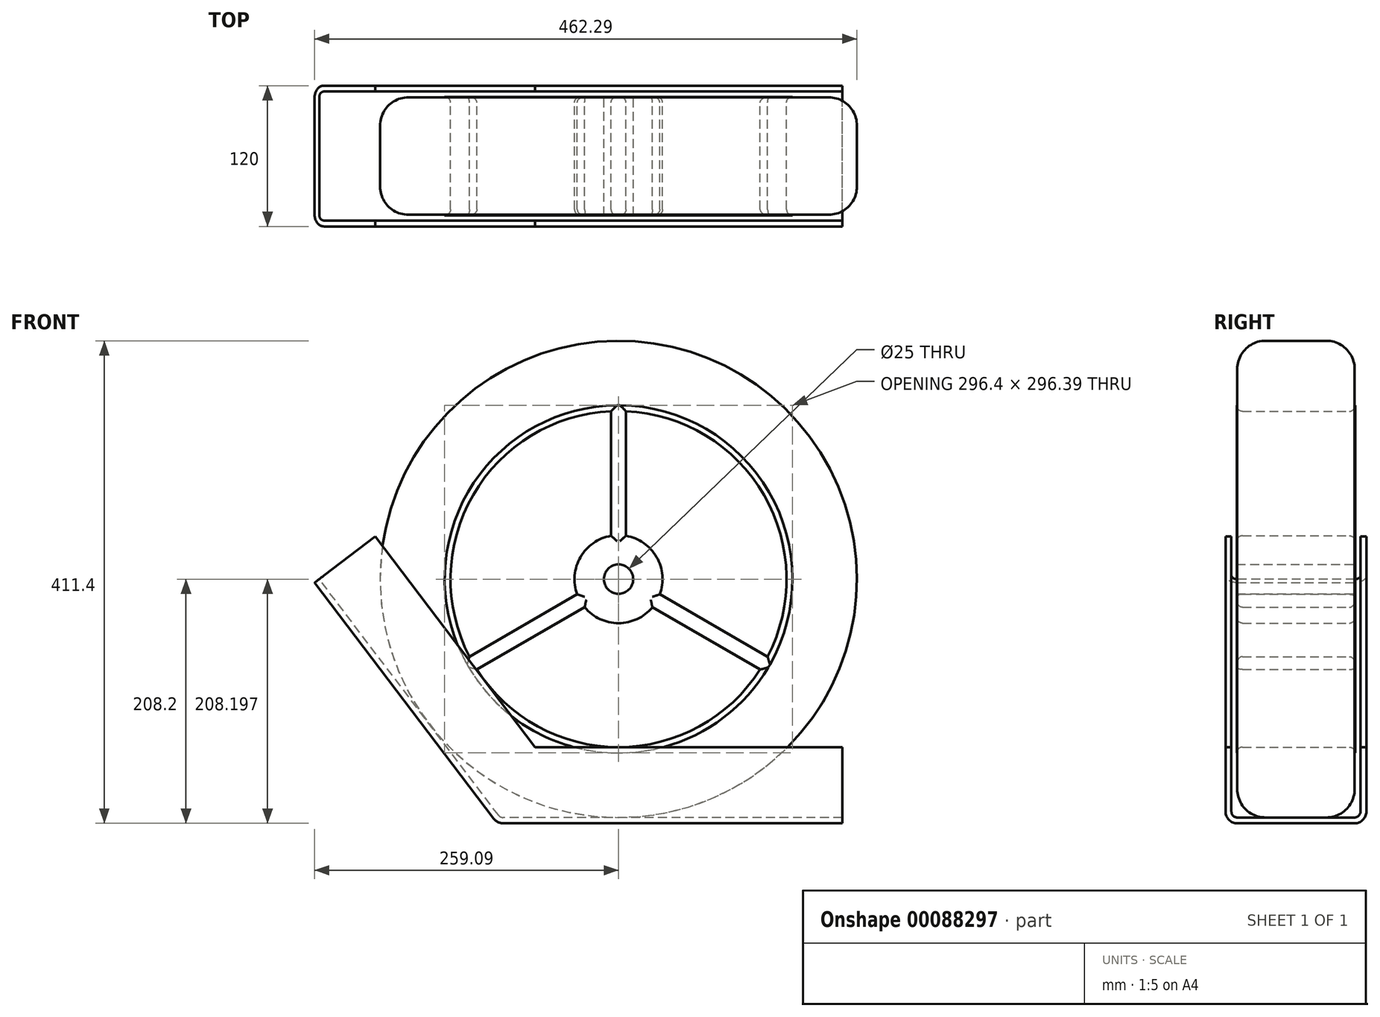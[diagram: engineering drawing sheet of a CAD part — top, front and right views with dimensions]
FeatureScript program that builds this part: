
annotation { "Feature Type Name" : "Feature", "Feature Type Description" : "" }
export const myFeature = defineFeature(function(context is Context, id is Id, definition is map)
    precondition{}
    {
        {
            var Q0;
            Q0=qCreatedBy(makeId("Front.planeOp"),FACE);
            var sketch = newSketch(context, id + "F0", { "sketchPlane" : qUnion([Q0])});
            skLineSegment(sketch, "E0", {"start": v(0, 0) * mm, "end": v(0, -208.26) * mm, "construction": true});
            skLineSegment(sketch, "E1", {"start": v(0, -203.2) * mm, "end": v(-100.87, -203.2) * mm});
            skLineSegment(sketch, "E2", {"start": v(0, -203.2) * mm, "end": v(190.72, -203.2) * mm});
            skLineSegment(sketch, "E3", {"start": v(-100.87, -203.2) * mm, "end": v(-255.1, 0) * mm});
            skLineSegment(sketch, "E4.0", {"start": v(-103.35, -208.2) * mm, "end": v(-259.09, -3.02) * mm});
            skLineSegment(sketch, "E4.1", {"start": v(0, -208.2) * mm, "end": v(-103.35, -208.2) * mm});
            skLineSegment(sketch, "E4.2", {"start": v(0, -208.2) * mm, "end": v(190.72, -208.2) * mm});
            skLineSegment(sketch, "E5", {"start": v(-259.09, -3.02) * mm, "end": v(-255.1, 0) * mm});
            skLineSegment(sketch, "E6", {"start": v(190.72, -203.2) * mm, "end": v(190.72, -208.2) * mm});
            skSolve(sketch);
        }
        {
            var Q0;
            Q0=makeQuery(id+"F0.imprint","IMPRINT",FACE,{"disambiguationData":[TD([[makeQuery(id+"F0.imprint","IMPRINT",EDGE,{"derivedFrom":sQuery(id+"F0.wireOp",EDGE,"E1")}),1.0]])]});
            extrude(context, id + "F1", {"entities" : qUnion([Q0]), "endBound" : BoundingType.SYMMETRIC, "depth" : 120 * mm});
        }
        {
            var Q0;
            Q0=makeQuery(id+"F1.opExtrude","SWEPT_FACE",FACE,{"disambiguationData":[OSD([sQuery(id+"F0.wireOp",EDGE,"E3")])]});
            extrude(context, id + "F2", {"entities" : qUnion([Q0]), "operationType" : NewBodyOperationType.ADD, "depth" : 60 * mm});
        }
        {
            var Q0;
            Q0=makeQuery(id+"F1.opExtrude","SWEPT_FACE",FACE,{"disambiguationData":[OSD([sQuery(id+"F0.wireOp",EDGE,"E1"),sQuery(id+"F0.wireOp",EDGE,"E2")])]});
            extrude(context, id + "F3", {"entities" : qUnion([Q0]), "operationType" : NewBodyOperationType.ADD, "depth" : 60 * mm});
        }
        {
            var Q0;
            Q0=makeQuery(id+"F2.opExtrude","CAP_FACE",FACE,{"disambiguationData":[OSD([sQuery(id+"F0.wireOp",EDGE,"E3")])],"isStart":false});
            var Q1;
            Q1=makeQuery(id+"F3.opExtrude","CAP_FACE",FACE,{"disambiguationData":[OSD([sQuery(id+"F0.wireOp",EDGE,"E1"),sQuery(id+"F0.wireOp",EDGE,"E2")])],"isStart":false});
            shell(context, id + "F4", {"entities" : qUnion([Q0, Q1]), "thickness" : 5 * mm});
        }
        {
            var Q0;
            {var subQ0=sQuery(id+"F0.wireOp",EDGE,"E6");Q0=makeQuery(id+"F3.boolean.opBoolean","MERGE",FACE,{"derivedFrom":[makeQuery(id+"F1.opExtrude","SWEPT_FACE",FACE,{"disambiguationData":[OSD([subQ0])]}),makeQuery(id+"F3.opExtrude","SWEPT_FACE",FACE,{"disambiguationData":[OSD([sQuery(id+"F0.wireOp",EDGE,"E2"),subQ0])]})]});}
            var sketch = newSketch(context, id + "F5", { "sketchPlane" : qUnion([Q0])});
            skLineSegment(sketch, "E7", {"start": v(-55, -143.2) * mm, "end": v(-55, -203.2) * mm});
            skLineSegment(sketch, "E8", {"start": v(-55, -203.2) * mm, "end": v(55, -203.2) * mm});
            skLineSegment(sketch, "E9", {"start": v(55, -203.2) * mm, "end": v(55, -143.2) * mm});
            skLineSegment(sketch, "E10", {"start": v(55, -143.2) * mm, "end": v(-55, -143.2) * mm});
            skSolve(sketch);
        }
        {
            var Q0;
            Q0=makeQuery(id+"F5.imprint","IMPRINT",FACE,{"disambiguationData":[TD([[makeQuery(id+"F5.imprint","IMPRINT",EDGE,{"derivedFrom":sQuery(id+"F5.wireOp",EDGE,"E7")}),1.0]])]});
            extrude(context, id + "F6", {"entities" : qUnion([Q0]), "operationType" : NewBodyOperationType.REMOVE, "oppositeDirection" : true, "depth" : 5 * mm});
        }
        {
            var Q0;
            {var subQ0=sQuery(id+"F0.wireOp",EDGE,"E5");Q0=makeQuery(id+"F2.boolean.opBoolean","MERGE",FACE,{"derivedFrom":[makeQuery(id+"F1.opExtrude","SWEPT_FACE",FACE,{"disambiguationData":[OSD([subQ0])]}),makeQuery(id+"F2.opExtrude","SWEPT_FACE",FACE,{"disambiguationData":[OSD([sQuery(id+"F0.wireOp",EDGE,"E3"),subQ0])]})]});}
            var sketch = newSketch(context, id + "F7", { "sketchPlane" : qUnion([Q0])});
            skLineSegment(sketch, "E11", {"start": v(-143.2, 55) * mm, "end": v(-203.2, 55) * mm});
            skLineSegment(sketch, "E12", {"start": v(-203.2, 55) * mm, "end": v(-203.2, -55) * mm});
            skLineSegment(sketch, "E13", {"start": v(-203.2, -55) * mm, "end": v(-143.2, -55) * mm});
            skSolve(sketch);
        }
        {
            var Q0;
            {var subQ0=sQuery(id+"F7.wireOp",EDGE,"E11");Q0=makeQuery(id+"F7.imprint","IMPRINT",FACE,{"disambiguationData":[TD([[makeQuery(id+"F7.imprint","IMPRINT",EDGE,{"derivedFrom":subQ0}),1.0]])]});}
            extrude(context, id + "F8", {"entities" : qUnion([Q0]), "operationType" : NewBodyOperationType.REMOVE, "oppositeDirection" : true, "depth" : 5 * mm});
        }
        {
            var Q0;
            Q0=qCreatedBy(makeId("Front.planeOp"),FACE);
            var sketch = newSketch(context, id + "F9", { "sketchPlane" : qUnion([Q0])});
            skCircle(sketch, "E14", {"center": v(0, 0) * mm, "radius": 203.2 * mm});
            skCircle(sketch, "E15", {"center": v(0, 0) * mm, "radius": 148.2 * mm});
            skSolve(sketch);
        }
        {
            var Q0;
            Q0=makeQuery(id+"F9.imprint","IMPRINT",FACE,{"disambiguationData":[TD([[makeQuery(id+"F9.imprint","IMPRINT",EDGE,{"derivedFrom":sQuery(id+"F9.wireOp",EDGE,"E14")}),1.0]])]});
            extrude(context, id + "F10", {"entities" : qUnion([Q0]), "operationType" : NewBodyOperationType.ADD, "endBound" : BoundingType.SYMMETRIC, "depth" : 100 * mm});
        }
        {
            var Q0;
            Q0=makeQuery(id+"F10.opExtrude","CAP_EDGE",EDGE,{"disambiguationData":[OSD([sQuery(id+"F9.wireOp",EDGE,"E14")])],"isStart":false});
            var Q1;
            Q1=makeQuery(id+"F10.opExtrude","CAP_EDGE",EDGE,{"disambiguationData":[OSD([sQuery(id+"F9.wireOp",EDGE,"E14")])],"isStart":true});
            fillet(context, id + "F11", {"entities" : qUnion([Q0, Q1]), "radius" : 24 * mm, "tangentPropagation" : true, "allowEdgeOverflow" : false});
        }
        {
            var Q0;
            Q0=makeQuery(id+"F1.opExtrude","CAP_EDGE",EDGE,{"disambiguationData":[OSD([sQuery(id+"F0.wireOp",EDGE,"E4.1"),sQuery(id+"F0.wireOp",EDGE,"E4.2")])],"isStart":false});
            var Q1;
            Q1=makeQuery(id+"F1.opExtrude","CAP_EDGE",EDGE,{"disambiguationData":[OSD([sQuery(id+"F0.wireOp",EDGE,"E4.1"),sQuery(id+"F0.wireOp",EDGE,"E4.2")])],"isStart":true});
            var Q2;
            Q2=makeQuery(id+"F1.opExtrude","CAP_EDGE",EDGE,{"disambiguationData":[OSD([sQuery(id+"F0.wireOp",EDGE,"E4.0")])],"isStart":true});
            var Q3;
            Q3=makeQuery(id+"F1.opExtrude","CAP_EDGE",EDGE,{"disambiguationData":[OSD([sQuery(id+"F0.wireOp",EDGE,"E4.0")])],"isStart":false});
            var Q4;
            Q4=makeQuery(id+"F1.opExtrude","SWEPT_EDGE",EDGE,{"disambiguationData":[OSD([sQuery(id+"F0.wireOp",EDGE,"E4.0"),sQuery(id+"F0.wireOp",EDGE,"E4.1")])]});
            fillet(context, id + "F12", {"entities" : qUnion([Q0, Q1, Q2, Q3, Q4]), "radius" : 10 * mm, "tangentPropagation" : true, "allowEdgeOverflow" : false});
        }
        {
            var Q0;
            {var subQ0=sQuery(id+"F0.wireOp",EDGE,"E4.2");var subQ1=sQuery(id+"F0.wireOp",EDGE,"E4.1");Q0=makeQuery(id+"F6.boolean.opBoolean","MERGE",EDGE,{"derivedFrom":[makeQuery(id+"F4.opShell","OFFSET_EDGE",EDGE,{"disambiguationData":[OSD([subQ1,subQ0]),TDD([makeQuery(id+"F1.opExtrude","CAP_EDGE",EDGE,{"disambiguationData":[OSD([subQ1,subQ0])],"isStart":false})])]}),makeQuery(id+"F6.opExtrude","SWEPT_EDGE",EDGE,{"disambiguationData":[OSD([sQuery(id+"F5.wireOp",EDGE,"E7"),sQuery(id+"F5.wireOp",EDGE,"E8")])]})]});}
            var Q1;
            {var subQ0=sQuery(id+"F0.wireOp",EDGE,"E4.2");var subQ1=sQuery(id+"F0.wireOp",EDGE,"E4.1");Q1=makeQuery(id+"F6.boolean.opBoolean","MERGE",EDGE,{"derivedFrom":[makeQuery(id+"F4.opShell","OFFSET_EDGE",EDGE,{"disambiguationData":[OSD([subQ1,subQ0]),TDD([makeQuery(id+"F1.opExtrude","CAP_EDGE",EDGE,{"disambiguationData":[OSD([subQ1,subQ0])],"isStart":true})])]}),makeQuery(id+"F6.opExtrude","SWEPT_EDGE",EDGE,{"disambiguationData":[OSD([sQuery(id+"F5.wireOp",EDGE,"E8"),sQuery(id+"F5.wireOp",EDGE,"E9")])]})]});}
            var Q2;
            Q2=makeQuery(id+"F4.opShell","OFFSET_EDGE",EDGE,{"disambiguationData":[OSD([sQuery(id+"F0.wireOp",EDGE,"E4.0"),sQuery(id+"F0.wireOp",EDGE,"E4.1")])]});
            var Q3;
            {var subQ0=sQuery(id+"F0.wireOp",EDGE,"E4.0");Q3=makeQuery(id+"F8.boolean.opBoolean","MERGE",EDGE,{"derivedFrom":[makeQuery(id+"F4.opShell","OFFSET_EDGE",EDGE,{"disambiguationData":[OSD([subQ0]),TDD([makeQuery(id+"F1.opExtrude","CAP_EDGE",EDGE,{"disambiguationData":[OSD([subQ0])],"isStart":false})])]}),makeQuery(id+"F8.opExtrude","SWEPT_EDGE",EDGE,{"disambiguationData":[OSD([sQuery(id+"F7.wireOp",EDGE,"E12"),sQuery(id+"F7.wireOp",EDGE,"E13")])]})]});}
            var Q4;
            {var subQ0=sQuery(id+"F0.wireOp",EDGE,"E4.0");Q4=makeQuery(id+"F8.boolean.opBoolean","MERGE",EDGE,{"derivedFrom":[makeQuery(id+"F4.opShell","OFFSET_EDGE",EDGE,{"disambiguationData":[OSD([subQ0]),TDD([makeQuery(id+"F1.opExtrude","CAP_EDGE",EDGE,{"disambiguationData":[OSD([subQ0])],"isStart":true})])]}),makeQuery(id+"F8.opExtrude","SWEPT_EDGE",EDGE,{"disambiguationData":[OSD([sQuery(id+"F7.wireOp",EDGE,"E11"),sQuery(id+"F7.wireOp",EDGE,"E12")])]})]});}
            fillet(context, id + "F13", {"entities" : qUnion([Q0, Q1, Q2, Q3, Q4]), "radius" : 5 * mm, "tangentPropagation" : true, "allowEdgeOverflow" : false});
        }
        {
            var Q0;
            Q0=qCreatedBy(makeId("Front.planeOp"),FACE);
            var sketch = newSketch(context, id + "F14", { "sketchPlane" : qUnion([Q0])});
            skCircle(sketch, "E16", {"center": v(0, 0) * mm, "radius": 143.2 * mm});
            skCircle(sketch, "E17", {"center": v(0, 0) * mm, "radius": 12.5 * mm});
            skCircle(sketch, "E18", {"center": v(0, 0) * mm, "radius": 37.5 * mm});
            skLineSegment(sketch, "E19", {"start": v(6.38, 36.95) * mm, "end": v(6.38, 143.06) * mm});
            skLineSegment(sketch, "E20", {"start": v(-6.38, 36.95) * mm, "end": v(-6.38, 143.06) * mm});
            skLineSegment(sketch, "E21.1.0", {"start": v(-35.2, -12.95) * mm, "end": v(-127.08, -66) * mm});
            skLineSegment(sketch, "E21.1.1", {"start": v(-28.81, -24) * mm, "end": v(-120.7, -77.05) * mm});
            skLineSegment(sketch, "E21.2.0", {"start": v(28.81, -24) * mm, "end": v(120.7, -77.05) * mm});
            skLineSegment(sketch, "E21.2.1", {"start": v(35.2, -12.95) * mm, "end": v(127.08, -66) * mm});
            skCircle(sketch, "E22.0", {"center": v(0, 0) * mm, "radius": 148.2 * mm});
            skSolve(sketch);
        }
        {
            var Q0;
            {var subQ0=sQuery(id+"F14.wireOp",EDGE,"E19");Q0=makeQuery(id+"F14.imprint","IMPRINT",FACE,{"disambiguationData":[TD([[makeQuery(id+"F14.imprint","IMPRINT",EDGE,{"derivedFrom":subQ0}),1.0]])]});}
            var Q1;
            {var subQ0=sQuery(id+"F14.wireOp",EDGE,"E21.2.0");Q1=makeQuery(id+"F14.imprint","IMPRINT",FACE,{"disambiguationData":[TD([[makeQuery(id+"F14.imprint","IMPRINT",EDGE,{"derivedFrom":subQ0}),1.0]])]});}
            var Q2;
            {var subQ0=sQuery(id+"F14.wireOp",EDGE,"E21.1.0");Q2=makeQuery(id+"F14.imprint","IMPRINT",FACE,{"disambiguationData":[TD([[makeQuery(id+"F14.imprint","IMPRINT",EDGE,{"derivedFrom":subQ0}),1.0]])]});}
            var Q3;
            Q3=makeQuery(id+"F14.imprint","IMPRINT",FACE,{"disambiguationData":[TD([[makeQuery(id+"F14.imprint","IMPRINT",EDGE,{"derivedFrom":sQuery(id+"F14.wireOp",EDGE,"E17")}),-1.0]])]});
            extrude(context, id + "F15", {"entities" : qUnion([Q0, Q1, Q2, Q3]), "endBound" : BoundingType.SYMMETRIC, "depth" : 101 * mm});
        }
        {
            var Q0;
            Q0=makeQuery(id+"F15.opExtrude","CAP_EDGE",EDGE,{"disambiguationData":[OSD([sQuery(id+"F14.wireOp",EDGE,"E19")])],"isStart":false});
            var Q1;
            Q1=makeQuery(id+"F15.opExtrude","CAP_EDGE",EDGE,{"disambiguationData":[OSD([sQuery(id+"F14.wireOp",EDGE,"E20")])],"isStart":false});
            var Q2;
            Q2=makeQuery(id+"F15.opExtrude","CAP_EDGE",EDGE,{"disambiguationData":[OSD([sQuery(id+"F14.wireOp",EDGE,"E21.2.1")])],"isStart":false});
            var Q3;
            Q3=makeQuery(id+"F15.opExtrude","CAP_EDGE",EDGE,{"disambiguationData":[OSD([sQuery(id+"F14.wireOp",EDGE,"E21.2.0")])],"isStart":false});
            var Q4;
            Q4=makeQuery(id+"F15.opExtrude","CAP_EDGE",EDGE,{"disambiguationData":[OSD([sQuery(id+"F14.wireOp",EDGE,"E21.1.1")])],"isStart":false});
            var Q5;
            Q5=makeQuery(id+"F15.opExtrude","CAP_EDGE",EDGE,{"disambiguationData":[OSD([sQuery(id+"F14.wireOp",EDGE,"E21.1.0")])],"isStart":false});
            var Q6;
            {var subQ0=sQuery(id+"F14.wireOp",EDGE,"E18");Q6=makeQuery(id+"F15.opExtrude","CAP_EDGE",EDGE,{"disambiguationData":[OSD([subQ0]),TDD([makeQuery(id+"F14.imprint","IMPRINT",EDGE,{"disambiguationData":[TD([[makeQuery(id+"F14.imprint","INTERSECT",VERTEX,{"derivedFrom":[sQuery(id+"F14.wireOp",EDGE,"E19"),subQ0]}),1.0]])],"derivedFrom":subQ0})])],"isStart":false});}
            var Q7;
            {var subQ0=sQuery(id+"F14.wireOp",EDGE,"E18");Q7=makeQuery(id+"F15.opExtrude","CAP_EDGE",EDGE,{"disambiguationData":[OSD([subQ0]),TDD([makeQuery(id+"F14.imprint","IMPRINT",EDGE,{"disambiguationData":[TD([[makeQuery(id+"F14.imprint","INTERSECT",VERTEX,{"derivedFrom":[sQuery(id+"F14.wireOp",EDGE,"E20"),subQ0]}),-1.0]])],"derivedFrom":subQ0})])],"isStart":false});}
            var Q8;
            {var subQ0=sQuery(id+"F14.wireOp",EDGE,"E18");Q8=makeQuery(id+"F15.opExtrude","CAP_EDGE",EDGE,{"disambiguationData":[OSD([subQ0]),TDD([makeQuery(id+"F14.imprint","IMPRINT",EDGE,{"disambiguationData":[TD([[makeQuery(id+"F14.imprint","INTERSECT",VERTEX,{"derivedFrom":[sQuery(id+"F14.wireOp",EDGE,"E21.1.1"),subQ0]}),-1.0]])],"derivedFrom":subQ0})])],"isStart":false});}
            var Q9;
            Q9=makeQuery(id+"F15.opExtrude","CAP_EDGE",EDGE,{"disambiguationData":[OSD([sQuery(id+"F14.wireOp",EDGE,"E21.1.1")])],"isStart":true});
            var Q10;
            Q10=makeQuery(id+"F15.opExtrude","CAP_EDGE",EDGE,{"disambiguationData":[OSD([sQuery(id+"F14.wireOp",EDGE,"E21.1.0")])],"isStart":true});
            var Q11;
            {var subQ0=sQuery(id+"F14.wireOp",EDGE,"E18");Q11=makeQuery(id+"F15.opExtrude","CAP_EDGE",EDGE,{"disambiguationData":[OSD([subQ0]),TDD([makeQuery(id+"F14.imprint","IMPRINT",EDGE,{"disambiguationData":[TD([[makeQuery(id+"F14.imprint","INTERSECT",VERTEX,{"derivedFrom":[sQuery(id+"F14.wireOp",EDGE,"E20"),subQ0]}),-1.0]])],"derivedFrom":subQ0})])],"isStart":true});}
            var Q12;
            Q12=makeQuery(id+"F15.opExtrude","CAP_EDGE",EDGE,{"disambiguationData":[OSD([sQuery(id+"F14.wireOp",EDGE,"E20")])],"isStart":true});
            var Q13;
            Q13=makeQuery(id+"F15.opExtrude","CAP_EDGE",EDGE,{"disambiguationData":[OSD([sQuery(id+"F14.wireOp",EDGE,"E19")])],"isStart":true});
            var Q14;
            {var subQ0=sQuery(id+"F14.wireOp",EDGE,"E18");Q14=makeQuery(id+"F15.opExtrude","CAP_EDGE",EDGE,{"disambiguationData":[OSD([subQ0]),TDD([makeQuery(id+"F14.imprint","IMPRINT",EDGE,{"disambiguationData":[TD([[makeQuery(id+"F14.imprint","INTERSECT",VERTEX,{"derivedFrom":[sQuery(id+"F14.wireOp",EDGE,"E19"),subQ0]}),1.0]])],"derivedFrom":subQ0})])],"isStart":true});}
            var Q15;
            Q15=makeQuery(id+"F15.opExtrude","CAP_EDGE",EDGE,{"disambiguationData":[OSD([sQuery(id+"F14.wireOp",EDGE,"E21.2.0")])],"isStart":true});
            var Q16;
            Q16=makeQuery(id+"F15.opExtrude","CAP_EDGE",EDGE,{"disambiguationData":[OSD([sQuery(id+"F14.wireOp",EDGE,"E21.2.1")])],"isStart":true});
            var Q17;
            {var subQ0=sQuery(id+"F14.wireOp",EDGE,"E18");Q17=makeQuery(id+"F15.opExtrude","CAP_EDGE",EDGE,{"disambiguationData":[OSD([subQ0]),TDD([makeQuery(id+"F14.imprint","IMPRINT",EDGE,{"disambiguationData":[TD([[makeQuery(id+"F14.imprint","INTERSECT",VERTEX,{"derivedFrom":[sQuery(id+"F14.wireOp",EDGE,"E21.1.1"),subQ0]}),-1.0]])],"derivedFrom":subQ0})])],"isStart":true});}
            fillet(context, id + "F16", {"entities" : qUnion([Q0, Q1, Q2, Q3, Q4, Q5, Q6, Q7, Q8, Q9, Q10, Q11, Q12, Q13, Q14, Q15, Q16, Q17]), "radius" : 5 * mm, "tangentPropagation" : true, "allowEdgeOverflow" : false});
        }
        {
            var Q0;
            Q0=makeQuery(id+"F14.imprint","IMPRINT",FACE,{"disambiguationData":[TD([[makeQuery(id+"F14.imprint","IMPRINT",EDGE,{"derivedFrom":sQuery(id+"F14.wireOp",EDGE,"E22.0")}),1.0]])]});
            extrude(context, id + "F17", {"entities" : qUnion([Q0]), "operationType" : NewBodyOperationType.ADD, "endBound" : BoundingType.SYMMETRIC, "depth" : 101 * mm});
        }
        {
            var Q0;
            {var subQ0=sQuery(id+"F14.wireOp",EDGE,"E16");var subQ2=sQuery(id+"F14.wireOp",EDGE,"E20");Q0=makeQuery(id+"F17.boolean.opBoolean","SPLIT",EDGE,{"disambiguationData":[TD([makeQuery(id+"F16.opFillet","BLEND_FACE",FACE,{"disambiguationData":[OSD([subQ2]),TDD([makeQuery(id+"F15.opExtrude","CAP_EDGE",EDGE,{"disambiguationData":[OSD([subQ2])],"isStart":false})])]})])],"derivedFrom":makeQuery(id+"F17.opExtrude","CAP_EDGE",EDGE,{"disambiguationData":[OSD([subQ0])],"isStart":false})});}
            var Q1;
            {var subQ0=sQuery(id+"F14.wireOp",EDGE,"E16");var subQ2=sQuery(id+"F14.wireOp",EDGE,"E19");Q1=makeQuery(id+"F17.boolean.opBoolean","SPLIT",EDGE,{"disambiguationData":[TD([makeQuery(id+"F16.opFillet","BLEND_FACE",FACE,{"disambiguationData":[OSD([subQ2]),TDD([makeQuery(id+"F15.opExtrude","CAP_EDGE",EDGE,{"disambiguationData":[OSD([subQ2])],"isStart":false})])]})])],"derivedFrom":makeQuery(id+"F17.opExtrude","CAP_EDGE",EDGE,{"disambiguationData":[OSD([subQ0])],"isStart":false})});}
            var Q2;
            {var subQ0=sQuery(id+"F14.wireOp",EDGE,"E16");var subQ2=sQuery(id+"F14.wireOp",EDGE,"E21.1.1");Q2=makeQuery(id+"F17.boolean.opBoolean","SPLIT",EDGE,{"disambiguationData":[TD([makeQuery(id+"F16.opFillet","BLEND_FACE",FACE,{"disambiguationData":[OSD([subQ2]),TDD([makeQuery(id+"F15.opExtrude","CAP_EDGE",EDGE,{"disambiguationData":[OSD([subQ2])],"isStart":false})])]})])],"derivedFrom":makeQuery(id+"F17.opExtrude","CAP_EDGE",EDGE,{"disambiguationData":[OSD([subQ0])],"isStart":false})});}
            var Q3;
            {var subQ0=sQuery(id+"F14.wireOp",EDGE,"E16");var subQ2=sQuery(id+"F14.wireOp",EDGE,"E20");Q3=makeQuery(id+"F17.boolean.opBoolean","SPLIT",EDGE,{"disambiguationData":[TD([makeQuery(id+"F16.opFillet","BLEND_FACE",FACE,{"disambiguationData":[OSD([subQ2]),TDD([makeQuery(id+"F15.opExtrude","CAP_EDGE",EDGE,{"disambiguationData":[OSD([subQ2])],"isStart":true})])]})])],"derivedFrom":makeQuery(id+"F17.opExtrude","CAP_EDGE",EDGE,{"disambiguationData":[OSD([subQ0])],"isStart":true})});}
            var Q4;
            {var subQ0=sQuery(id+"F14.wireOp",EDGE,"E16");var subQ1=sQuery(id+"F14.wireOp",EDGE,"E21.1.1");Q4=makeQuery(id+"F17.boolean.opBoolean","SPLIT",EDGE,{"disambiguationData":[TD([makeQuery(id+"F16.opFillet","BLEND_FACE",FACE,{"disambiguationData":[OSD([subQ1]),TDD([makeQuery(id+"F15.opExtrude","CAP_EDGE",EDGE,{"disambiguationData":[OSD([subQ1])],"isStart":true})])]})])],"derivedFrom":makeQuery(id+"F17.opExtrude","CAP_EDGE",EDGE,{"disambiguationData":[OSD([subQ0])],"isStart":true})});}
            var Q5;
            {var subQ0=sQuery(id+"F14.wireOp",EDGE,"E16");var subQ1=sQuery(id+"F14.wireOp",EDGE,"E19");Q5=makeQuery(id+"F17.boolean.opBoolean","SPLIT",EDGE,{"disambiguationData":[TD([makeQuery(id+"F16.opFillet","BLEND_FACE",FACE,{"disambiguationData":[OSD([subQ1]),TDD([makeQuery(id+"F15.opExtrude","CAP_EDGE",EDGE,{"disambiguationData":[OSD([subQ1])],"isStart":true})])]})])],"derivedFrom":makeQuery(id+"F17.opExtrude","CAP_EDGE",EDGE,{"disambiguationData":[OSD([subQ0])],"isStart":true})});}
            fillet(context, id + "F18", {"entities" : qUnion([Q0, Q1, Q2, Q3, Q4, Q5]), "radius" : 5 * mm, "tangentPropagation" : true, "allowEdgeOverflow" : false});
        }
        {
            var Q0;
            Q0=makeQuery(id+"F9.imprint","IMPRINT",FACE,{"disambiguationData":[TD([[makeQuery(id+"F9.imprint","IMPRINT",EDGE,{"derivedFrom":sQuery(id+"F9.wireOp",EDGE,"E15")}),1.0]])]});
            var Q1;
            Q1=sQuery(id+"F9.wireOp",EDGE,"E15");
            extrude(context, id + "F19", {"entities" : qUnion([Q0]), "bodyType" : ToolBodyType.SURFACE, "operationType" : NewBodyOperationType.ADD, "surfaceEntities" : qUnion([Q1]), "endBound" : BoundingType.SYMMETRIC, "depth" : 100 * mm});
        }
    });
